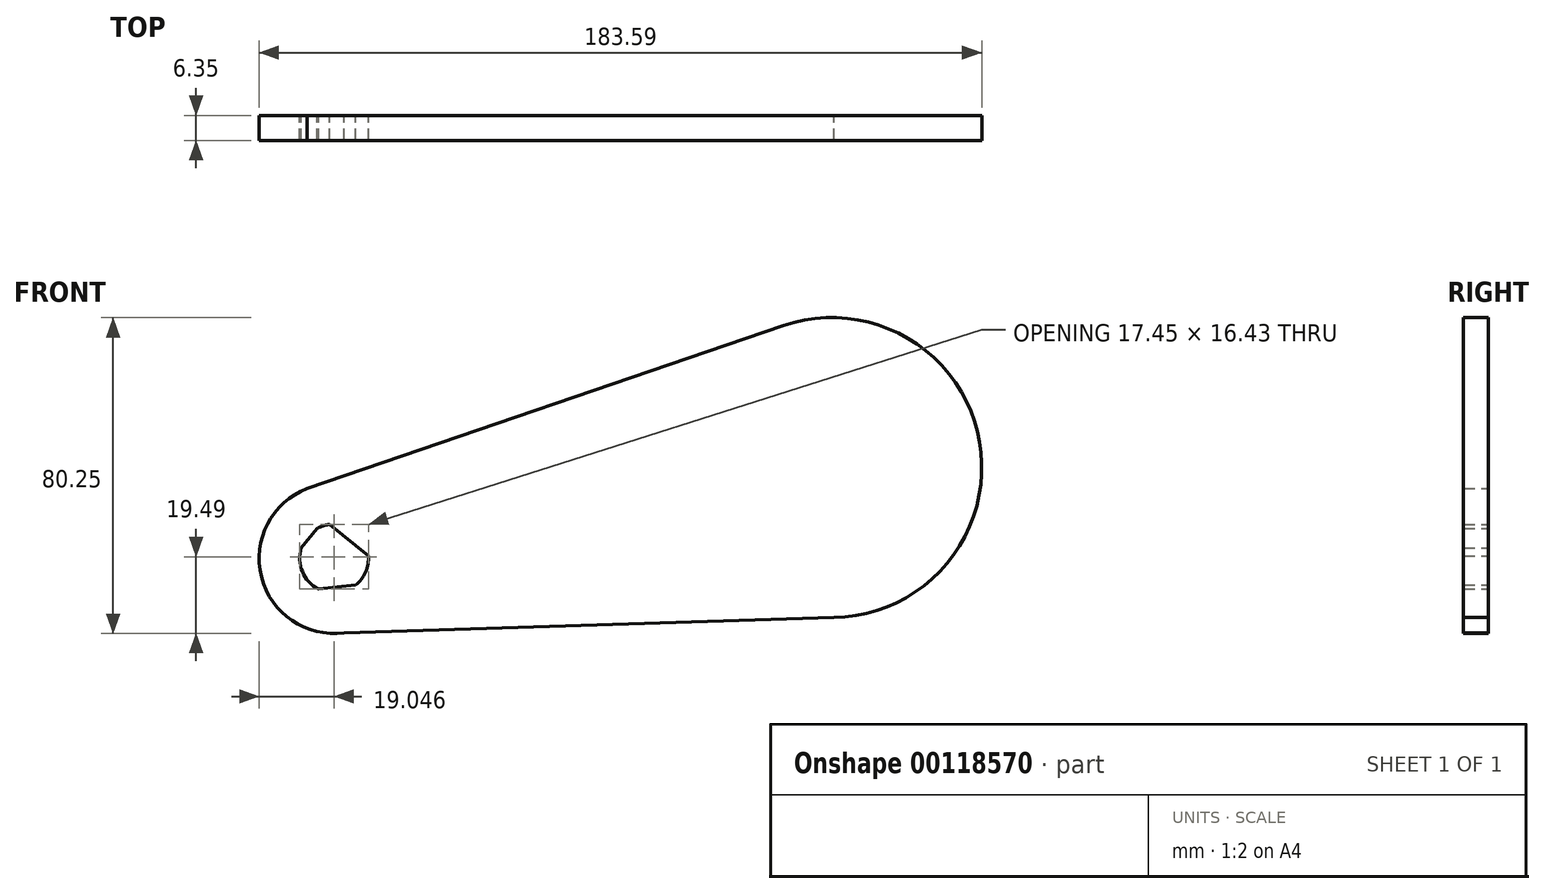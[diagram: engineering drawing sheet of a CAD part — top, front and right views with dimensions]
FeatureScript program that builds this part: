
annotation { "Feature Type Name" : "Feature", "Feature Type Description" : "" }
export const myFeature = defineFeature(function(context is Context, id is Id, definition is map)
    precondition{}
    {
        {
            var Q0;
            Q0=qCreatedBy(makeId("Front.planeOp"),FACE);
            var sketch = newSketch(context, id + "F0", { "sketchPlane" : qUnion([Q0])});
            skArc(sketch, "E0", {"start": v(31.76, 6.35) * mm, "mid": v(30.13, 5.97) * mm, "end": v(28.6, 5.29) * mm});
            skLineSegment(sketch, "E1", {"start": v(31.76, 6.35) * mm, "end": v(41.63, -1.64) * mm});
            skLineSegment(sketch, "E2", {"start": v(28.6, 5.29) * mm, "end": v(24.6, 0.35) * mm});
            skLineSegment(sketch, "E3", {"start": v(28.95, -10.07) * mm, "end": v(38.43, -9.08) * mm});
            skArc(sketch, "E4.trimOffspring", {"start": v(38.43, -9.08) * mm, "mid": v(40.95, -5.75) * mm, "end": v(41.63, -1.64) * mm});
            skArc(sketch, "E5.trimOffspring", {"start": v(24.6, 0.35) * mm, "mid": v(24.87, -5.66) * mm, "end": v(28.95, -10.07) * mm});
            skArc(sketch, "E6", {"start": v(26.06, 15.47) * mm, "mid": v(14.47, -7) * mm, "end": v(35.42, -21.19) * mm});
            skLineSegment(sketch, "E7", {"start": v(26.06, 15.47) * mm, "end": v(147.04, 56.85) * mm});
            skLineSegment(sketch, "E8", {"start": v(35.42, -21.19) * mm, "end": v(159.9, -17.3) * mm});
            skArc(sketch, "E9", {"start": v(159.9, -17.3) * mm, "mid": v(196.9, 27.3) * mm, "end": v(147.04, 56.85) * mm});
            skSolve(sketch);
        }
        {
            var Q0;
            Q0=makeQuery(id+"F0.imprint","IMPRINT",FACE,{"disambiguationData":[TD([[makeQuery(id+"F0.imprint","IMPRINT",EDGE,{"derivedFrom":sQuery(id+"F0.wireOp",EDGE,"E0")}),-1.0]])]});
            extrude(context, id + "F1", {"entities" : qUnion([Q0]), "depth" : 6.35 * mm});
        }
    });
